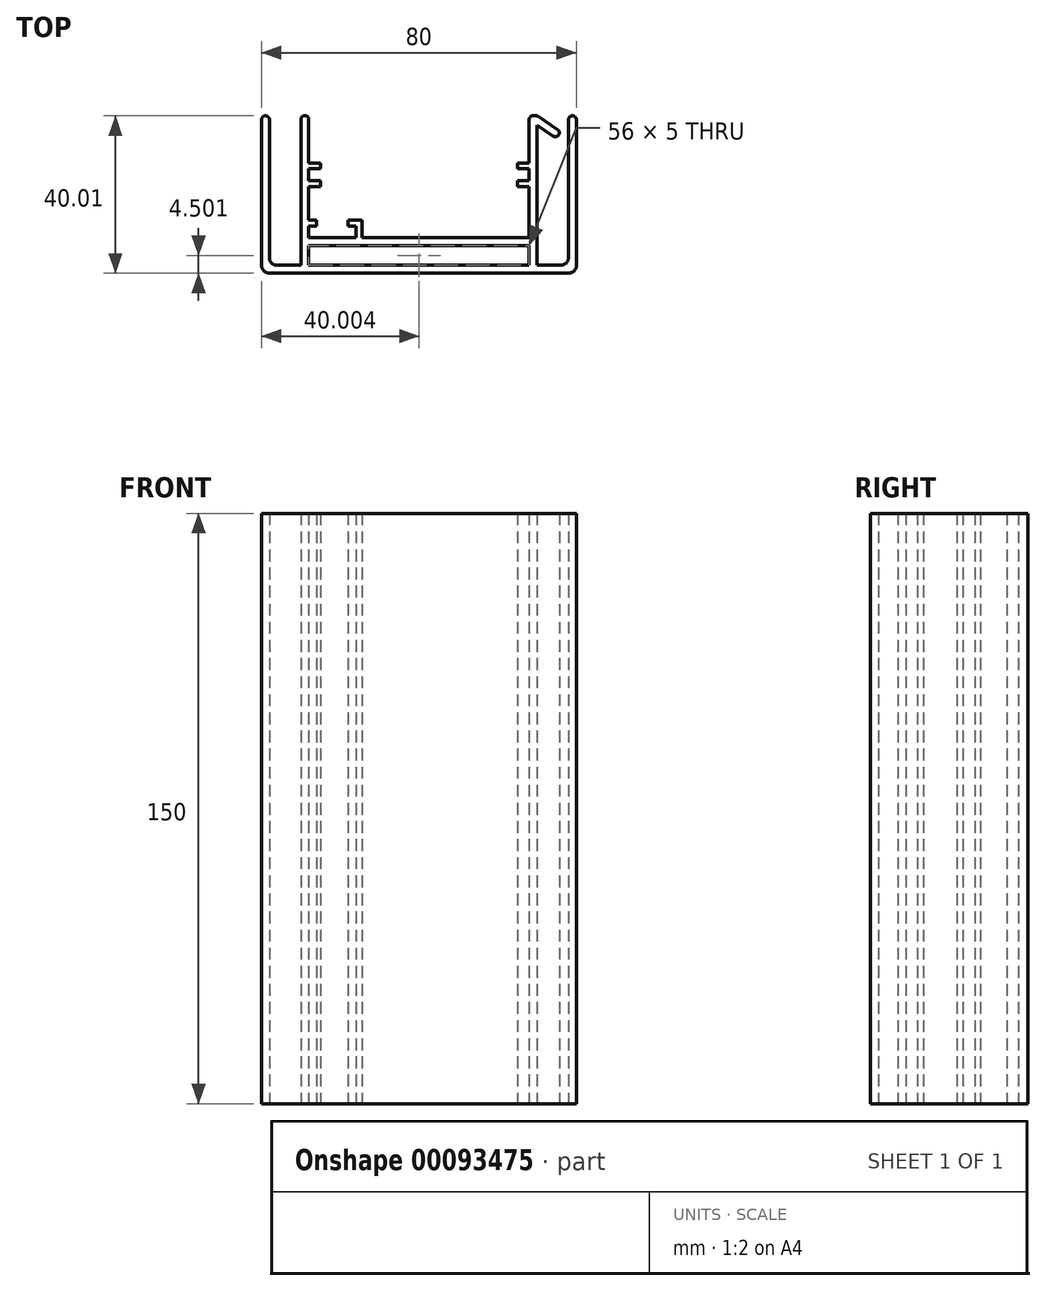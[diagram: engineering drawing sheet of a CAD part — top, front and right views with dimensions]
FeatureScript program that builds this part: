
annotation { "Feature Type Name" : "Feature", "Feature Type Description" : "" }
export const myFeature = defineFeature(function(context is Context, id is Id, definition is map)
    precondition{}
    {
        {
            var Q0;
            Q0=qCreatedBy(makeId("Top.planeOp"),FACE);
            var sketch = newSketch(context, id + "F0", { "sketchPlane" : qUnion([Q0])});
            skLineSegment(sketch, "E0", {"start": v(-38.78, -31.44) * mm, "end": v(37.22, -31.44) * mm});
            skLineSegment(sketch, "E1", {"start": v(39.22, -29.44) * mm, "end": v(39.22, 8.56) * mm});
            skLineSegment(sketch, "E2", {"start": v(29.22, -29.44) * mm, "end": v(29.22, 8.57) * mm});
            skLineSegment(sketch, "E3", {"start": v(-40.78, -29.44) * mm, "end": v(-40.78, 8.56) * mm});
            skLineSegment(sketch, "E4", {"start": v(-30.78, -29.44) * mm, "end": v(-30.78, 8.57) * mm});
            skLineSegment(sketch, "E5.0", {"start": v(-38.78, -27.44) * mm, "end": v(-38.78, 8.56) * mm});
            skLineSegment(sketch, "E5.1", {"start": v(-36.78, -29.44) * mm, "end": v(-30.78, -29.44) * mm});
            skLineSegment(sketch, "E5.2", {"start": v(37.22, -27.44) * mm, "end": v(37.22, 8.56) * mm});
            skLineSegment(sketch, "E6", {"start": v(-28.78, -3.43) * mm, "end": v(-25.78, -3.43) * mm});
            skLineSegment(sketch, "E7.0", {"start": v(-28.78, -4.93) * mm, "end": v(-25.78, -4.93) * mm});
            skLineSegment(sketch, "E8.0", {"start": v(-28.78, -7.93) * mm, "end": v(-25.78, -7.93) * mm});
            skLineSegment(sketch, "E9.0", {"start": v(-28.78, -9.43) * mm, "end": v(-25.78, -9.43) * mm});
            skLineSegment(sketch, "E10", {"start": v(-25.78, -3.43) * mm, "end": v(-25.78, -4.93) * mm});
            skLineSegment(sketch, "E11", {"start": v(24.22, -3.43) * mm, "end": v(24.22, -4.93) * mm});
            skLineSegment(sketch, "E12", {"start": v(-40.78, 8.56) * mm, "end": v(-38.78, 8.56) * mm});
            skLineSegment(sketch, "E13", {"start": v(-30.78, 8.57) * mm, "end": v(-28.78, 8.57) * mm});
            skLineSegment(sketch, "E14", {"start": v(37.22, 8.56) * mm, "end": v(39.22, 8.56) * mm});
            skLineSegment(sketch, "E15", {"start": v(27.22, 8.57) * mm, "end": v(29.22, 8.57) * mm});
            skPoint(sketch, "E16.visualSharp", {"position": v(-38.78, -29.44) * mm});
            skArc(sketch, "E16.filletArc", {"start": v(-38.78, -27.44) * mm, "mid": v(-38.19, -28.85) * mm, "end": v(-36.78, -29.44) * mm});
            skPoint(sketch, "E17.visualSharp", {"position": v(-40.78, -31.44) * mm});
            skArc(sketch, "E17.filletArc", {"start": v(-40.78, -29.44) * mm, "mid": v(-40.19, -30.85) * mm, "end": v(-38.78, -31.44) * mm});
            skPoint(sketch, "E18.visualSharp", {"position": v(39.22, -31.44) * mm});
            skArc(sketch, "E18.filletArc", {"start": v(37.22, -31.44) * mm, "mid": v(38.64, -30.85) * mm, "end": v(39.22, -29.44) * mm});
            skArc(sketch, "E19.filletArc", {"start": v(35.22, -29.44) * mm, "mid": v(36.64, -28.85) * mm, "end": v(37.22, -27.44) * mm});
            skLineSegment(sketch, "E20.trimOffspring", {"start": v(-28.78, -29.44) * mm, "end": v(-28.78, -26.44) * mm});
            skLineSegment(sketch, "E21.trimOffspring", {"start": v(-28.78, -24.94) * mm, "end": v(-28.78, -24.44) * mm});
            skLineSegment(sketch, "E22.trimOffspring", {"start": v(-28.78, -7.93) * mm, "end": v(-28.78, -4.93) * mm});
            skLineSegment(sketch, "E23.trimOffspring", {"start": v(-28.78, -3.43) * mm, "end": v(-28.78, 8.57) * mm});
            skLineSegment(sketch, "E24.trimOffspring", {"start": v(24.22, -4.93) * mm, "end": v(27.22, -4.93) * mm});
            skLineSegment(sketch, "E25.trimOffspring", {"start": v(24.22, -3.43) * mm, "end": v(27.22, -3.43) * mm});
            skLineSegment(sketch, "E26.trimOffspring", {"start": v(24.22, -7.93) * mm, "end": v(27.22, -7.93) * mm});
            skLineSegment(sketch, "E27.trimOffspring", {"start": v(24.22, -9.43) * mm, "end": v(27.22, -9.43) * mm});
            skLineSegment(sketch, "E28.trimOffspring", {"start": v(24.22, -7.93) * mm, "end": v(24.22, -9.43) * mm});
            skLineSegment(sketch, "E29.trimOffspring", {"start": v(-25.78, -7.93) * mm, "end": v(-25.78, -9.43) * mm});
            skLineSegment(sketch, "E30.trimOffspring", {"start": v(27.22, -3.43) * mm, "end": v(27.22, 8.57) * mm});
            skLineSegment(sketch, "E31.trimOffspring", {"start": v(27.22, -29.44) * mm, "end": v(27.22, -9.43) * mm});
            skLineSegment(sketch, "E32.trimOffspring", {"start": v(29.22, -29.44) * mm, "end": v(35.22, -29.44) * mm});
            skLineSegment(sketch, "E33.trimOffspring", {"start": v(-28.78, -29.44) * mm, "end": v(-16.78, -29.44) * mm});
            skLineSegment(sketch, "E34.trimOffspring", {"start": v(-15.28, -29.44) * mm, "end": v(27.22, -29.44) * mm});
            skLineSegment(sketch, "E35", {"start": v(27.22, -4.93) * mm, "end": v(27.22, -7.93) * mm});
            skLineSegment(sketch, "E36", {"start": v(-28.78, -24.44) * mm, "end": v(27.22, -24.44) * mm});
            skLineSegment(sketch, "E37.0", {"start": v(-28.78, -22.44) * mm, "end": v(-16.78, -22.44) * mm});
            skLineSegment(sketch, "E38", {"start": v(-16.78, -19.44) * mm, "end": v(-18.78, -19.44) * mm});
            skLineSegment(sketch, "E39", {"start": v(-28.78, -19.44) * mm, "end": v(-26.78, -19.44) * mm});
            skLineSegment(sketch, "E40.0", {"start": v(-15.28, -17.94) * mm, "end": v(-18.78, -17.94) * mm});
            skLineSegment(sketch, "E41", {"start": v(-26.78, -19.44) * mm, "end": v(-26.78, -17.94) * mm});
            skLineSegment(sketch, "E42", {"start": v(-18.78, -17.94) * mm, "end": v(-18.78, -19.44) * mm});
            skLineSegment(sketch, "E43.trimOffspring", {"start": v(-28.78, -17.94) * mm, "end": v(-26.78, -17.94) * mm});
            skLineSegment(sketch, "E44", {"start": v(-28.78, -24.94) * mm, "end": v(-28.78, -26.44) * mm});
            skLineSegment(sketch, "E45", {"start": v(-16.78, -29.44) * mm, "end": v(-15.28, -29.44) * mm});
            skLineSegment(sketch, "E46", {"start": v(-15.28, -17.94) * mm, "end": v(-15.28, -22.44) * mm});
            skLineSegment(sketch, "E47", {"start": v(-16.78, -19.44) * mm, "end": v(-16.78, -22.44) * mm});
            skLineSegment(sketch, "E48.trimOffspring", {"start": v(-28.78, -17.94) * mm, "end": v(-28.78, -9.43) * mm});
            skLineSegment(sketch, "E49.trimOffspring", {"start": v(-28.78, -22.44) * mm, "end": v(-28.78, -19.44) * mm});
            skLineSegment(sketch, "E50.trimOffspring", {"start": v(-15.28, -22.44) * mm, "end": v(27.22, -22.44) * mm});
            skLineSegment(sketch, "E51", {"start": v(29.22, 8.57) * mm, "end": v(35.26, 4.53) * mm});
            skLineSegment(sketch, "E52.0", {"start": v(29.22, 6.16) * mm, "end": v(34.14, 2.87) * mm});
            skLineSegment(sketch, "E53", {"start": v(35.26, 4.53) * mm, "end": v(34.14, 2.87) * mm});
            skSolve(sketch);
        }
        {
            var Q0;
            {var subQ0=sQuery(id+"F0.wireOp",EDGE,"E51");Q0=makeQuery(id+"F0.imprint","IMPRINT",FACE,{"disambiguationData":[TD([[makeQuery(id+"F0.imprint","IMPRINT",EDGE,{"derivedFrom":subQ0}),-1.0]])]});}
            var Q1;
            Q1=makeQuery(id+"F0.imprint","IMPRINT",FACE,{"disambiguationData":[TD([[makeQuery(id+"F0.imprint","IMPRINT",EDGE,{"derivedFrom":sQuery(id+"F0.wireOp",EDGE,"E0")}),1.0]])]});
            extrude(context, id + "F1", {"entities" : qUnion([Q0, Q1]), "depth" : 150 * mm});
        }
        {
            var Q0;
            Q0=makeQuery(id+"F1.opExtrude","SWEPT_EDGE",EDGE,{"disambiguationData":[OSD([sQuery(id+"F0.wireOp",EDGE,"E3"),sQuery(id+"F0.wireOp",EDGE,"E12")])]});
            var Q1;
            Q1=makeQuery(id+"F1.opExtrude","SWEPT_EDGE",EDGE,{"disambiguationData":[OSD([sQuery(id+"F0.wireOp",EDGE,"E5.0"),sQuery(id+"F0.wireOp",EDGE,"E12")])]});
            var Q2;
            Q2=makeQuery(id+"F1.opExtrude","SWEPT_EDGE",EDGE,{"disambiguationData":[OSD([sQuery(id+"F0.wireOp",EDGE,"E4"),sQuery(id+"F0.wireOp",EDGE,"E13")])]});
            var Q3;
            Q3=makeQuery(id+"F1.opExtrude","SWEPT_EDGE",EDGE,{"disambiguationData":[OSD([sQuery(id+"F0.wireOp",EDGE,"E13"),sQuery(id+"F0.wireOp",EDGE,"E23.trimOffspring")])]});
            var Q4;
            Q4=makeQuery(id+"F1.opExtrude","SWEPT_EDGE",EDGE,{"disambiguationData":[OSD([sQuery(id+"F0.wireOp",EDGE,"E15"),sQuery(id+"F0.wireOp",EDGE,"E30.trimOffspring")])]});
            var Q5;
            Q5=makeQuery(id+"F1.opExtrude","SWEPT_EDGE",EDGE,{"disambiguationData":[OSD([sQuery(id+"F0.wireOp",EDGE,"E2"),sQuery(id+"F0.wireOp",EDGE,"E15"),sQuery(id+"F0.wireOp",EDGE,"E51")])]});
            var Q6;
            Q6=makeQuery(id+"F1.opExtrude","SWEPT_EDGE",EDGE,{"disambiguationData":[OSD([sQuery(id+"F0.wireOp",EDGE,"E51"),sQuery(id+"F0.wireOp",EDGE,"E53")])]});
            var Q7;
            Q7=makeQuery(id+"F1.opExtrude","SWEPT_EDGE",EDGE,{"disambiguationData":[OSD([sQuery(id+"F0.wireOp",EDGE,"E52.0"),sQuery(id+"F0.wireOp",EDGE,"E53")])]});
            var Q8;
            Q8=makeQuery(id+"F1.opExtrude","SWEPT_EDGE",EDGE,{"disambiguationData":[OSD([sQuery(id+"F0.wireOp",EDGE,"E5.2"),sQuery(id+"F0.wireOp",EDGE,"E14")])]});
            var Q9;
            Q9=makeQuery(id+"F1.opExtrude","SWEPT_EDGE",EDGE,{"disambiguationData":[OSD([sQuery(id+"F0.wireOp",EDGE,"E1"),sQuery(id+"F0.wireOp",EDGE,"E14")])]});
            fillet(context, id + "F2", {"entities" : qUnion([Q0, Q1, Q2, Q3, Q4, Q5, Q6, Q7, Q8, Q9]), "radius" : 1 * mm, "tangentPropagation" : true, "allowEdgeOverflow" : false});
        }
    });
